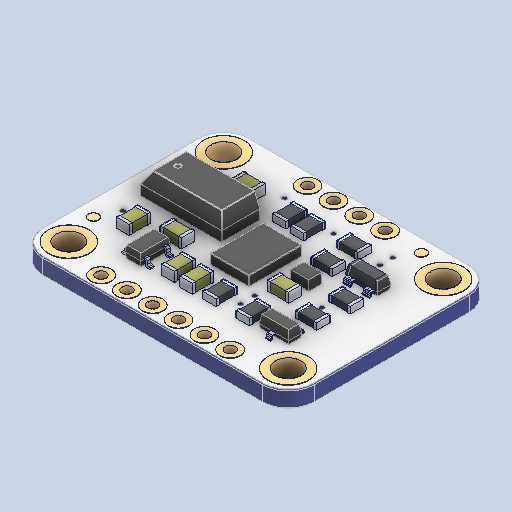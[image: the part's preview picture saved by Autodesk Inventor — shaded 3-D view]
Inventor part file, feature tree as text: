
AUTODESK INVENTOR PART (.ipt)
format: ipt  version: 2024.2 (Build 282272000, 272)  size: 824,320 bytes
history: native  units: in
note: dims shown in document units (in); Inventor stores cm internally (conversion verified against a paired STEP export)
features: other x71, mirror x19, fillet x2, chamfer x2
ambient origin geometry x8: Origin, YZ Plane, XZ Plane, XY Plane, X Axis, Y Axis, Z Axis, Center Point
bodies: Solid1 (feature_tree), Solid2 (feature_tree), Solid3 (feature_tree), Solid4 (feature_tree), Solid5 (feature_tree), Solid6 (feature_tree), Solid7 (feature_tree), Solid8 (feature_tree), Solid9 (feature_tree), Solid10 (feature_tree), Solid11 (feature_tree), Solid12 (feature_tree), Solid13 (feature_tree), Solid14 (feature_tree), Solid15 (feature_tree), Solid16 (feature_tree), Solid17 (feature_tree), Solid18 (feature_tree), Solid19 (feature_tree), Solid20 (feature_tree), Solid21 (feature_tree), Solid22 (feature_tree), Solid23 (feature_tree), Solid24 (feature_tree), Solid25 (feature_tree), Solid26 (feature_tree), Solid27 (feature_tree), Solid28 (feature_tree), Solid29 (feature_tree), Solid30 (feature_tree), Solid31 (feature_tree), Solid32 (feature_tree), Solid33 (feature_tree), Solid34 (feature_tree), Solid35 (feature_tree), Solid36 (feature_tree), Solid37 (feature_tree), Solid38 (feature_tree), Solid39 (feature_tree), Solid40 (feature_tree), Solid41 (feature_tree), Solid42 (feature_tree), Solid43 (feature_tree), Solid44 (feature_tree), Solid45 (feature_tree), Solid46 (feature_tree), Solid47 (feature_tree), Solid48 (feature_tree), Solid49 (feature_tree), Solid50 (feature_tree), Solid51 (feature_tree), Solid52 (feature_tree), Solid53 (feature_tree), Solid54 (feature_tree), Solid55 (feature_tree), Solid56 (feature_tree), Solid57 (feature_tree), Solid58 (feature_tree), Solid59 (feature_tree), Solid60 (feature_tree), Solid61 (feature_tree), Solid62 (feature_tree), Solid63 (feature_tree), Solid64 (feature_tree), Solid65 (feature_tree), Solid66 (feature_tree), Solid67 (feature_tree), Solid68 (feature_tree), Solid69 (feature_tree), Solid70 (feature_tree), Solid71 (feature_tree), Solid72 (feature_tree), Solid73 (feature_tree), Solid74 (feature_tree), Solid75 (feature_tree), Solid76 (feature_tree), Solid77 (feature_tree), Solid78 (feature_tree), Solid79 (feature_tree), Solid80 (feature_tree), Solid81 (feature_tree), Solid82 (feature_tree), Solid83 (feature_tree), Solid84 (feature_tree), Solid85 (feature_tree), Solid86 (feature_tree), Solid87 (feature_tree), Solid88 (feature_tree), Solid89 (feature_tree), Solid90 (feature_tree), Solid91 (feature_tree), Solid92 (feature_tree), Solid93 (feature_tree), Solid94 (feature_tree)
feature tree (94):
  fillet  "Fillet2"  [1 undecoded]
  other  "Boss-Extrude4[1]"
  other  "Boss-Extrude4[2]"
  other  "Boss-Extrude4[3]"
  other  "Boss-Extrude4[4]"
  other  "Boss-Extrude4[5]"
  other  "Boss-Extrude4[6]"
  other  "Boss-Extrude5[1]"
  other  "Boss-Extrude5[2]"
  other  "Boss-Extrude5[3]"
  other  "Boss-Extrude5[4]"
  other  "Boss-Extrude5[5]"
  other  "Boss-Extrude5[6]"
  other  "Boss-Extrude5[7]"
  other  "Boss-Extrude5[8]"
  chamfer  "Chamfer4"  [1 undecoded]
  other  "Boss-Extrude7[1]"
  other  "Boss-Extrude7[2]"
  other  "LPattern3[1]"
  other  "LPattern3[2]"
  other  "LPattern4"
  chamfer  "Chamfer6"  [1 undecoded]
  other  "Boss-Extrude9"
  other  "LPattern5"
  other  "LPattern6"
  mirror  "Mirror1"
  mirror  "Mirror2[1]"
  mirror  "Mirror2[2]"
  mirror  "Mirror2[3]"
  mirror  "Mirror2[4]"
  other  "LPattern9[1]"
  other  "LPattern9[2]"
  other  "LPattern9[3]"
  other  "LPattern9[4]"
  other  "Boss-Extrude10[1]"
  other  "Boss-Extrude10[2]"
  other  "Boss-Extrude10[3]"
  other  "Boss-Extrude10[4]"
  other  "Boss-Extrude10[5]"
  other  "Boss-Extrude10[6]"
  other  "Boss-Extrude10[7]"
  other  "Boss-Extrude10[8]"
  other  "Boss-Extrude10[9]"
  other  "Boss-Extrude10[10]"
  other  "Boss-Extrude10[11]"
  other  "Boss-Extrude10[12]"
  other  "Boss-Extrude10[13]"
  other  "Boss-Extrude10[14]"
  other  "Boss-Extrude10[15]"
  other  "Boss-Extrude10[16]"
  mirror  "Mirror3[1]"
  mirror  "Mirror3[2]"
  mirror  "Mirror3[3]"
  mirror  "Mirror3[4]"
  mirror  "Mirror3[5]"
  mirror  "Mirror3[6]"
  mirror  "Mirror3[7]"
  mirror  "Mirror3[8]"
  mirror  "Mirror3[9]"
  mirror  "Mirror3[10]"
  mirror  "Mirror3[11]"
  mirror  "Mirror3[12]"
  mirror  "Mirror3[13]"
  mirror  "Mirror3[14]"
  fillet  "Fillet10"  [1 undecoded]
  other  "Boss-Extrude11[1]"
  other  "Boss-Extrude11[2]"
  other  "Boss-Extrude11[3]"
  other  "Boss-Extrude11[4]"
  other  "Boss-Extrude11[5]"
  other  "Boss-Extrude11[6]"
  other  "Boss-Extrude11[7]"
  other  "Boss-Extrude11[8]"
  other  "Boss-Extrude11[9]"
  other  "Boss-Extrude11[10]"
  other  "Boss-Extrude11[11]"
  other  "Boss-Extrude11[12]"
  other  "Boss-Extrude11[13]"
  other  "Boss-Extrude11[14]"
  other  "Boss-Extrude11[15]"
  other  "Boss-Extrude11[16]"
  other  "Boss-Extrude12[1]"
  other  "Boss-Extrude12[2]"
  other  "Boss-Extrude12[3]"
  other  "Boss-Extrude12[4]"
  other  "Boss-Extrude12[5]"
  other  "Boss-Extrude12[6]"
  other  "Boss-Extrude12[7]"
  other  "Boss-Extrude12[8]"
  other  "Boss-Extrude12[9]"
  other  "Boss-Extrude12[10]"
  other  "Boss-Extrude12[11]"
  other  "Boss-Extrude12[12]"
  other  "Boss-Extrude13"
note: 4 required parameter values undecoded (feature->parameter linkage not recoverable at this tier; creation-order binding heuristic only, values carry confidence <= 0.55)
